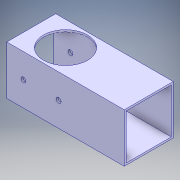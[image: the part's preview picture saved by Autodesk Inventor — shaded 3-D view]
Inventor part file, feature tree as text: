
AUTODESK INVENTOR PART (.ipt)
format: ipt  version: 2018 (Build 220112000, 112)  size: 134,144 bytes
history: native  units: mm
features: other x2, extrude x1, sketch x1
ambient origin geometry x8: Origin, YZ Plane, XZ Plane, XY Plane, X Axis, Y Axis, Z Axis, Center Point
bodies: Body1 (feature_tree)
feature tree (4):
  other  "ソリッド1"
  extrude  "押し出し1"  Depth=50.0mm
  sketch  "スケッチ1"
  other  "PartBody"
